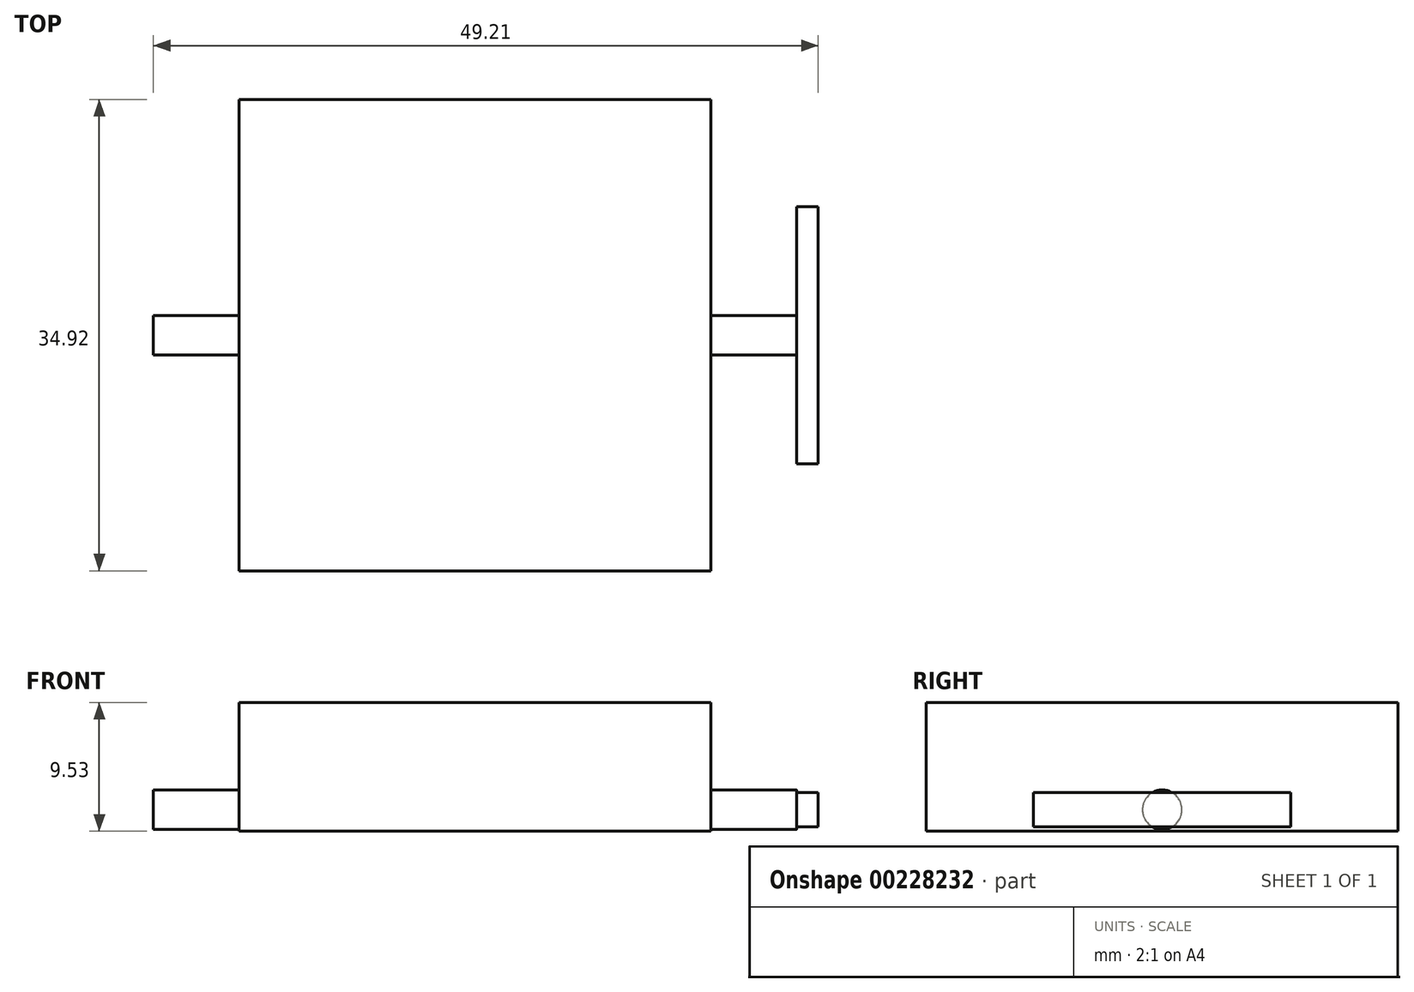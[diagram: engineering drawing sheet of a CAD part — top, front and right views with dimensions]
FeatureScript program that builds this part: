
annotation { "Feature Type Name" : "Feature", "Feature Type Description" : "" }
export const myFeature = defineFeature(function(context is Context, id is Id, definition is map)
    precondition{}
    {
        {
            var Q0;
            Q0=qCreatedBy(makeId("Top.planeOp"),FACE);
            var sketch = newSketch(context, id + "F0", { "sketchPlane" : qUnion([Q0])});
            skLineSegment(sketch, "E0.bottom", {"start": v(-15.87, 15.88) * mm, "end": v(15.88, 15.88) * mm});
            skLineSegment(sketch, "E0.top", {"start": v(-15.88, -15.88) * mm, "end": v(15.87, -15.88) * mm});
            skLineSegment(sketch, "E0.left", {"start": v(-15.88, 15.88) * mm, "end": v(-15.88, -15.88) * mm});
            skLineSegment(sketch, "E0.right", {"start": v(15.88, 15.88) * mm, "end": v(15.87, -15.88) * mm});
            skPoint(sketch, "E0.middle", {"position": v(0, 0) * mm});
            skLineSegment(sketch, "E1.bottom", {"start": v(-17.46, 17.46) * mm, "end": v(17.46, 17.46) * mm});
            skLineSegment(sketch, "E1.top", {"start": v(-17.46, -17.46) * mm, "end": v(17.46, -17.46) * mm});
            skLineSegment(sketch, "E1.left", {"start": v(-17.46, 17.46) * mm, "end": v(-17.46, -17.46) * mm});
            skLineSegment(sketch, "E1.right", {"start": v(17.46, 17.46) * mm, "end": v(17.46, -17.46) * mm});
            skLineSegment(sketch, "E2", {"start": v(17.46, 0) * mm, "end": v(23.81, 0) * mm});
            skLineSegment(sketch, "E3.bottom", {"start": v(23.81, 1.46) * mm, "end": v(17.46, 1.46) * mm});
            skLineSegment(sketch, "E3.top", {"start": v(23.81, -1.46) * mm, "end": v(17.46, -1.46) * mm});
            skLineSegment(sketch, "E3.left", {"start": v(23.81, 1.46) * mm, "end": v(23.81, -1.46) * mm});
            skLineSegment(sketch, "E3.right", {"start": v(17.46, 1.46) * mm, "end": v(17.46, -1.46) * mm});
            skPoint(sketch, "E3.middle", {"position": v(20.64, 0) * mm});
            skLineSegment(sketch, "E4.MirrorCS", {"start": v(-23.81, 1.46) * mm, "end": v(-17.46, 1.46) * mm});
            skLineSegment(sketch, "E5.MirrorCS", {"start": v(-17.46, 0) * mm, "end": v(-23.81, 0) * mm});
            skLineSegment(sketch, "E6.MirrorCS", {"start": v(-23.81, -1.46) * mm, "end": v(-17.46, -1.46) * mm});
            skLineSegment(sketch, "E7.MirrorCS", {"start": v(-23.81, 1.46) * mm, "end": v(-23.81, -1.46) * mm});
            skSolve(sketch);
        }
        {
            var Q0;
            Q0=makeQuery(id+"F0.imprint","IMPRINT",FACE,{"disambiguationData":[TD([[makeQuery(id+"F0.imprint","IMPRINT",EDGE,{"derivedFrom":sQuery(id+"F0.wireOp",EDGE,"E0.bottom")}),1.0]])]});
            var Q1;
            Q1=makeQuery(id+"F0.imprint","IMPRINT",FACE,{"disambiguationData":[TD([[makeQuery(id+"F0.imprint","IMPRINT",EDGE,{"derivedFrom":sQuery(id+"F0.wireOp",EDGE,"E0.bottom")}),-1.0]])]});
            extrude(context, id + "F1", {"entities" : qUnion([Q0, Q1]), "endBound" : BoundingType.SYMMETRIC, "depth" : 3.17 * mm});
        }
        {
            var Q0;
            {var subQ0=sQuery(id+"F0.wireOp",EDGE,"E4.MirrorCS");Q0=makeQuery(id+"F0.imprint","IMPRINT",FACE,{"disambiguationData":[TD([[makeQuery(id+"F0.imprint","IMPRINT",EDGE,{"derivedFrom":subQ0}),-1.0]])]});}
            var Q1;
            {var subQ0=sQuery(id+"F0.wireOp",EDGE,"E5.MirrorCS");Q1=makeQuery(id+"F0.imprint","IMPRINT",FACE,{"disambiguationData":[TD([[makeQuery(id+"F0.imprint","IMPRINT",EDGE,{"derivedFrom":subQ0}),1.0]])]});}
            var Q2;
            {var subQ0=sQuery(id+"F0.wireOp",EDGE,"E2");Q2=makeQuery(id+"F0.imprint","IMPRINT",FACE,{"disambiguationData":[TD([[makeQuery(id+"F0.imprint","IMPRINT",EDGE,{"derivedFrom":subQ0}),1.0]])]});}
            var Q3;
            {var subQ0=sQuery(id+"F0.wireOp",EDGE,"E2");Q3=makeQuery(id+"F0.imprint","IMPRINT",FACE,{"disambiguationData":[TD([[makeQuery(id+"F0.imprint","IMPRINT",EDGE,{"derivedFrom":subQ0}),-1.0]])]});}
            extrude(context, id + "F2", {"entities" : qUnion([Q0, Q1, Q2, Q3]), "operationType" : NewBodyOperationType.ADD, "endBound" : BoundingType.SYMMETRIC, "depth" : 2.92 * mm});
        }
        {
            var Q0;
            Q0=makeQuery(id+"F2.opExtrude","CAP_EDGE",EDGE,{"disambiguationData":[OSD([sQuery(id+"F0.wireOp",EDGE,"E6.MirrorCS")])],"isStart":false});
            var Q1;
            Q1=makeQuery(id+"F2.opExtrude","CAP_EDGE",EDGE,{"disambiguationData":[OSD([sQuery(id+"F0.wireOp",EDGE,"E4.MirrorCS")])],"isStart":false});
            var Q2;
            Q2=makeQuery(id+"F2.opExtrude","CAP_EDGE",EDGE,{"disambiguationData":[OSD([sQuery(id+"F0.wireOp",EDGE,"E6.MirrorCS")])],"isStart":true});
            var Q3;
            Q3=makeQuery(id+"F2.opExtrude","CAP_EDGE",EDGE,{"disambiguationData":[OSD([sQuery(id+"F0.wireOp",EDGE,"E4.MirrorCS")])],"isStart":true});
            var Q4;
            Q4=makeQuery(id+"F2.opExtrude","CAP_EDGE",EDGE,{"disambiguationData":[OSD([sQuery(id+"F0.wireOp",EDGE,"E3.bottom")])],"isStart":true});
            var Q5;
            Q5=makeQuery(id+"F2.opExtrude","CAP_EDGE",EDGE,{"disambiguationData":[OSD([sQuery(id+"F0.wireOp",EDGE,"E3.top")])],"isStart":true});
            var Q6;
            Q6=makeQuery(id+"F2.opExtrude","CAP_EDGE",EDGE,{"disambiguationData":[OSD([sQuery(id+"F0.wireOp",EDGE,"E3.top")])],"isStart":false});
            var Q7;
            Q7=makeQuery(id+"F2.opExtrude","CAP_EDGE",EDGE,{"disambiguationData":[OSD([sQuery(id+"F0.wireOp",EDGE,"E3.bottom")])],"isStart":false});
            fillet(context, id + "F3", {"entities" : qUnion([Q0, Q1, Q2, Q3, Q4, Q5, Q6, Q7]), "radius" : 1.46 * mm, "tangentPropagation" : true, "allowEdgeOverflow" : false});
        }
        {
            var Q0;
            Q0=makeQuery(id+"F2.opExtrude","SWEPT_FACE",FACE,{"disambiguationData":[OSD([sQuery(id+"F0.wireOp",EDGE,"E3.left")])]});
            var sketch = newSketch(context, id + "F4", { "sketchPlane" : qUnion([Q0])});
            skLineSegment(sketch, "E8.bottom", {"start": v(-9.52, 1.27) * mm, "end": v(9.53, 1.27) * mm});
            skLineSegment(sketch, "E8.top", {"start": v(-9.52, -1.27) * mm, "end": v(9.53, -1.27) * mm});
            skLineSegment(sketch, "E8.left", {"start": v(-9.52, 1.27) * mm, "end": v(-9.52, -1.27) * mm});
            skLineSegment(sketch, "E8.right", {"start": v(9.53, 1.27) * mm, "end": v(9.53, -1.27) * mm});
            skPoint(sketch, "E8.middle", {"position": v(0, 0) * mm});
            skSolve(sketch);
        }
        {
            var Q0;
            {var subQ0=sQuery(id+"F4.wireOp",EDGE,"E8.bottom");var subQ1=makeQuery(id+"FDSBcHxy4eiEb2w_1.opExtrude","CAP_EDGE",EDGE,{"disambiguationData":[OSD([sQuery(id+"F0.wireOp",EDGE,"E3.top"),sQuery(id+"F0.wireOp",EDGE,"E3.left")])],"isStart":false});var subQ2=makeQuery(id+"F4.imprint","INTERSECT",VERTEX,{"disambiguationData":[OD(0.0)],"derivedFrom":[subQ1,subQ0]});Q0=makeQuery(id+"F4.imprint","IMPRINT",FACE,{"disambiguationData":[TD([[makeQuery(id+"F4.imprint","IMPRINT",EDGE,{"disambiguationData":[TD([[subQ2,-1.0]])],"derivedFrom":subQ0}),-1.0]])]});}
            var Q1;
            {var subQ0=sQuery(id+"F4.wireOp",EDGE,"E8.right");Q1=makeQuery(id+"F4.imprint","IMPRINT",FACE,{"disambiguationData":[TD([[makeQuery(id+"F4.imprint","IMPRINT",EDGE,{"derivedFrom":subQ0}),-1.0]])]});}
            var Q2;
            {var subQ0=sQuery(id+"F4.wireOp",EDGE,"E8.left");Q2=makeQuery(id+"F4.imprint","IMPRINT",FACE,{"disambiguationData":[TD([[makeQuery(id+"F4.imprint","IMPRINT",EDGE,{"derivedFrom":subQ0}),1.0]])]});}
            var Q3;
            {var subQ0=sQuery(id+"F4.wireOp",EDGE,"E8.bottom");var subQ1=makeQuery(id+"F3.opFillet","BLEND_EDGE",EDGE,{"blendedFrom":[makeQuery(id+"F2.opExtrude","CAP_EDGE",EDGE,{"disambiguationData":[OSD([sQuery(id+"F0.wireOp",EDGE,"E3.top")])],"isStart":false}),makeQuery(id+"F2.opExtrude","SWEPT_FACE",FACE,{"disambiguationData":[OSD([sQuery(id+"F0.wireOp",EDGE,"E3.left")])]})],"blendedInto":[makeQuery(id+"F2.opExtrude","SWEPT_FACE",FACE,{"disambiguationData":[OSD([sQuery(id+"F0.wireOp",EDGE,"E3.left")])]})]});var subQ2=makeQuery(id+"F4.imprint","INTERSECT",VERTEX,{"disambiguationData":[OD(0.0)],"derivedFrom":[subQ1,subQ0]});Q3=makeQuery(id+"F4.imprint","IMPRINT",FACE,{"disambiguationData":[TD([[makeQuery(id+"F4.imprint","IMPRINT",EDGE,{"disambiguationData":[TD([[subQ2,-1.0]])],"derivedFrom":subQ0}),-1.0]])]});}
            extrude(context, id + "F5", {"entities" : qUnion([Q0, Q1, Q2, Q3]), "operationType" : NewBodyOperationType.ADD, "depth" : 1.59 * mm});
        }
        {
            var Q0;
            Q0=makeQuery(id+"F1.opExtrude","CAP_FACE",FACE,{"disambiguationData":[OSD([sQuery(id+"F0.wireOp",EDGE,"E1.bottom"),sQuery(id+"F0.wireOp",EDGE,"E1.top"),sQuery(id+"F0.wireOp",EDGE,"E1.left"),sQuery(id+"F0.wireOp",EDGE,"E1.right"),sQuery(id+"F0.wireOp",EDGE,"E3.right")])],"isStart":false});
            extrude(context, id + "F6", {"entities" : qUnion([Q0]), "operationType" : NewBodyOperationType.ADD, "depth" : 6.35 * mm});
        }
    });
